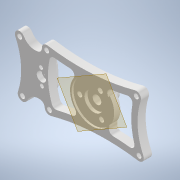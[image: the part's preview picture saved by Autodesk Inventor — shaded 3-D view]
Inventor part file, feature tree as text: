
AUTODESK INVENTOR PART (.ipt)
format: ipt  version: 2022 (Build 260153070, 153G)  size: 428,544 bytes
history: native  units: mm
features: reference x25, sketch x7, extrude x7, other x6, plane x5, projected_geometry x2
ambient origin geometry x8: Origin, YZ Plane, XZ Plane, XY Plane, X Axis, Y Axis, Z Axis, Center Point
bodies: Body1 (feature_tree)
feature tree (52):
  plane  "Work Plane1"
  sketch  "Sketch1"  dims[d0=1.0mm d1=10.0mm]
  plane  "Work Plane2"
  plane  "Work Plane3"
  extrude  "Extrusion2"  Depth=10.0mm
  extrude  "Extrusion3"  Depth=2.5mm
  extrude  "Extrusion4"  Depth=3.1mm
  sketch  "Sketch5"  dims[d9=1.5mm d12=57.25mm]
  plane  "Work Plane4"
  extrude  "Extrusion5"  Depth=57.25mm
  plane  "Work Plane5"
  extrude  "Extrusion6"  Depth=10.0mm TaperAngle=0.0deg
  extrude  "Extrusion7"  Depth=2.0mm TaperAngle=0.0deg
  extrude  "Extrusion8"  Depth=10.0mm
  reference  "Reference1"
  reference  "Reference2"
  reference  "Reference5"
  reference  "Reference6"
  reference  "Reference7"
  reference  "Reference8"
  reference  "Reference9"
  reference  "Reference10"
  reference  "Reference11"
  reference  "Reference12"
  reference  "Reference13"
  reference  "Reference14"
  reference  "Reference15"
  reference  "Reference16"
  reference  "Reference17"
  reference  "Reference18"
  reference  "Reference19"
  reference  "Reference20"
  reference  "Reference21"
  reference  "Reference22"
  sketch  "Sketch3"  dims[d2=2.5mm d3=2.5mm]
  reference  "Reference27"
  reference  "Reference29"
  reference  "Reference30"
  reference  "Reference32"
  projected_geometry  "Projected Loop3"
  sketch  "Sketch4"  dims[d4=3.1mm d5=3.1mm]
  projected_geometry  "Projected Loop4"
  sketch  "Sketch6"  dims[d13=3.05mm d14=10.0mm d15=0.0mm]
  reference  "Reference33"
  sketch  "Sketch7"  dims[d17=0.25mm d18=2.0mm d19=0.0mm]
  sketch  "Sketch8"  dims[d20=3.5mm d21=5.5mm d22=2.0mm d23=0.0mm d24=18.0mm d25=3.0mm d26=2.0mm d27=0.0mm d28=10.0mm d29=0.0mm d30=0.15mm d31=1.25mm d32=10.0mm d33=0.0mm d34=4.0mm d35=4.0mm d36=4.0mm d37=6.125278mm d38=1.0mm d39=10.0mm d40=0.0mm d41=0.5mm d42=0.872665mm d43=0.5mm d44=0.872665mm]
  other  "<userpath> laptop\Desktop\SumoBot\sumobotLIDAR\AssemblyV3.iam"
  other  "AssemblyV3.iam"
  other  "SRM-12-06A:1"
  other  "MOTOR:1"
  other  "AS5600_mount:1"
  other  "608ZZ bearing:1"
